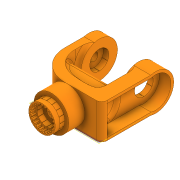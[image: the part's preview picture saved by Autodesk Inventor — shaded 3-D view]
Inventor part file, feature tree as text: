
AUTODESK INVENTOR PART (.ipt)
format: ipt  version: 2020 (Build 240168000, 168)  size: 1,737,216 bytes
history: native  units: in
note: dims shown in document units (in); Inventor stores cm internally (conversion verified against a paired STEP export)
features: sketch x34, extrude x33, projected_geometry x27, chamfer x5, plane x5, fillet x5
ambient origin geometry x8: Origin, YZ Plane, XZ Plane, XY Plane, X Axis, Y Axis, Z Axis, Center Point
bodies: Solid1 (feature_tree)
feature tree (109):
  extrude  "Extrusion1"  Depth=2.0472in
  extrude  "Extrusion2"  Depth=1.1024in
  chamfer  "Chamfer2"  Distance=0.2756in
  extrude  "Extrusion4"  Depth=0.0157in
  extrude  "Extrusion7"  Depth=0.2756in TaperAngle=0.0deg
  chamfer  "Chamfer4"  Distance=0.0394in
  extrude  "Extrusion8"  Depth=0.315in
  sketch  "Sketch12"  dims[d39=1.4567in d57=0.0394in d58=0.0in]
  plane  "Work Plane1"
  sketch  "Sketch13"  dims[d59=0.315in d60=0.125in d61=0.0137in d67=0.0157in]
  extrude  "Extrusion10"  Depth=0.0394in TaperAngle=0.0deg
  extrude  "Extrusion11"  Depth=0.0866in
  chamfer  "Chamfer5"  Distance=9.4488in Angle=360.0deg
  extrude  "Extrusion12"  Depth=0.2756in TaperAngle=0.0deg
  plane  "Work Plane2"
  extrude  "Extrusion13"  Depth=0.2756in
  plane  "Work Plane3"
  extrude  "Extrusion14"  Depth=1.0236in
  extrude  "Extrusion15"  Depth=0.8858in
  extrude  "Extrusion16"  Depth=0.3937in
  extrude  "Extrusion17"  Depth=1.378in
  sketch  "Sketch21"  dims[d107=0.2756in d108=0.0in d109=0.2756in d110=0.125in d111=0.0137in]
  extrude  "Extrusion19"  Depth=0.5906in
  sketch  "Sketch23"  dims[d112=1.0in d113=0.0in d114=1.0236in]
  extrude  "Extrusion20"  Depth=0.1575in TaperAngle=0.0deg
  extrude  "Extrusion21"  Depth=0.1575in TaperAngle=0.0deg
  extrude  "Extrusion22"  Depth=4.2323in
  extrude  "Extrusion23"  Depth=0.1575in
  extrude  "Extrusion24"  Depth=1.1024in
  extrude  "Extrusion25"  Depth=0.4921in
  extrude  "Extrusion26"  Depth=0.75in
  extrude  "Extrusion27"  Depth=0.1575in TaperAngle=0.0deg
  extrude  "Extrusion28"  Depth=0.1575in
  extrude  "Extrusion29"  Depth=0.1575in
  plane  "Work Plane4"
  extrude  "Extrusion30"  Depth=0.315in TaperAngle=0.0deg
  fillet  "Fillet1"  Radius=0.3937in
  fillet  "Fillet2"  Radius=0.315in
  extrude  "Extrusion31"  Depth=0.315in TaperAngle=0.0deg
  extrude  "Extrusion32"  Depth=0.315in TaperAngle=0.0deg
  extrude  "Extrusion33"  Depth=0.3937in TaperAngle=0.0deg
  fillet  "Fillet3"  Radius=0.2165in
  extrude  "Extrusion34"  [1 undecoded]
  chamfer  "Chamfer6"  Distance=0.4724in
  chamfer  "Chamfer7"  Distance=0.2756in
  extrude  "Extrusion35"  Depth=0.315in
  extrude  "Extrusion36"  Depth=0.315in
  plane  "Work Plane5"
  fillet  "Fillet5"  Radius=0.0394in
  extrude  "Extrusion38"  Depth=0.315in TaperAngle=0.0deg
  extrude  "Extrusion39"  Depth=0.315in
  fillet  "Fillet6"  Radius=0.001in
  sketch  "Sketch1"  dims[d0=0.6299in d1=2.0472in]
  sketch  "Sketch2"  dims[d2=0.9449in d3=0.0in d4=1.1024in]
  sketch  "Sketch4"  dims[d5=1.5748in d6=0.2756in d7=0.0in]
  sketch  "Sketch8"  dims[d11=0.2756in d12=0.125in d13=0.0137in d25=0.0157in]
  projected_geometry  "Projected Loop2"
  sketch  "Sketch10"  dims[d26=6.2992in d28=360.0deg d30=0.2756in d31=0.0in]
  sketch  "Sketch14"  dims[d68=4.7244in d70=360.0deg d72=0.0394in d73=0.0in]
  sketch  "Sketch15"  dims[d83=0.0591in d84=0.0866in]
  projected_geometry  "Projected Loop4"
  sketch  "Sketch16"  dims[d85=0.0827in]
  sketch  "Sketch17"  dims[d86=0.0827in]
  projected_geometry  "Projected Loop5"
  sketch  "Sketch18"  dims[d87=0.0827in d88=9.4488in d90=360.0deg]
  projected_geometry  "Projected Loop6"
  projected_geometry  "Projected Loop7"
  sketch  "Sketch19"  dims[d92=0.2756in]
  projected_geometry  "Projected Loop8"
  projected_geometry  "Projected Loop9"
  sketch  "Sketch20"  dims[d94=9.4488in d95=0.0827in d96=0.0827in d97=0.0827in d98=360.0deg d105=0.2756in d106=0.0in]
  projected_geometry  "Projected Loop10"
  projected_geometry  "Projected Loop11"
  projected_geometry  "Projected Loop12"
  projected_geometry  "Projected Loop13"
  sketch  "Sketch25"  dims[d115=0.7874in d117=0.8858in]
  sketch  "Sketch26"  dims[d118=2.7559in d119=0.3937in]
  projected_geometry  "Projected Loop16"
  projected_geometry  "Projected Loop17"
  sketch  "Sketch27"  dims[d120=0.5906in d121=1.378in]
  projected_geometry  "Projected Loop18"
  projected_geometry  "Projected Loop19"
  sketch  "Sketch28"  dims[d123=3.4941in d124=0.5906in]
  projected_geometry  "Projected Loop20"
  projected_geometry  "Projected Loop21"
  sketch  "Sketch29"  dims[d126=1.9685in d129=0.1575in d130=0.0in]
  projected_geometry  "Projected Loop22"
  projected_geometry  "Projected Loop23"
  sketch  "Sketch30"  dims[d131=-2.0472in d132=0.1575in d133=0.0in]
  projected_geometry  "Projected Loop24"
  sketch  "Sketch31"  dims[d134=2.126in d136=4.2323in]
  sketch  "Sketch32"  dims[d137=0.1575in d138=0.1575in]
  sketch  "Sketch34"  dims[d139=0.4921in d140=0.0in d141=1.1024in]
  projected_geometry  "Projected Loop25"
  sketch  "Sketch35"  dims[d142=1.1614in d143=0.4921in]
  sketch  "Sketch36"  dims[d144=0.3445in d145=0.75in]
  projected_geometry  "Projected Loop26"
  sketch  "Sketch37"  dims[d146=0.1575in d147=0.0in d148=0.2165in d149=0.0in]
  projected_geometry  "Projected Loop27"
  sketch  "Sketch38"  dims[d152=1.0039in d153=0.0in d154=0.1575in]
  projected_geometry  "Projected Loop28"
  sketch  "Sketch39"  dims[d155=0.1575in d160=1.1811in]
  projected_geometry  "Projected Loop29"
  sketch  "Sketch40"  dims[d161=0.1969in d162=0.0in d163=0.315in d164=0.0in d165=0.3937in d166=0.0in d167=0.315in d168=0.0in]
  sketch  "Sketch41"  dims[d169=0.315in d170=0.0in d171=0.315in d172=0.0in]
  projected_geometry  "Projected Loop30"
  sketch  "Sketch43"  dims[d173=0.315in d174=0.0in d175=0.315in d176=0.0in]
  projected_geometry  "Projected Loop31"
  sketch  "Sketch44"  dims[d177=1.1024in d178=0.3937in d179=0.0in d180=0.2165in d181=0.0in d183=-0.0197in d184=0.4724in d185=0.2756in d186=0.0in d187=0.5512in d188=0.2165in d189=0.0394in d190=0.0in d191=0.0394in d192=0.0in d193=0.001in d194=0.001in d195=1.0in d196=0.0in d197=0.1575in d198=1.0in d199=0.0in d200=0.315in d201=0.125in d202=0.0137in d203=0.315in d204=0.125in d205=0.0137in d206=0.0157in d207=2.3622in d209=360.0deg d211=1.0in d212=0.0in d213=1.0in d214=0.0in d215=-0.0787in d221=0.1969in d222=0.1969in d223=0.0in d224=0.1575in d225=0.1575in d226=0.1969in d227=0.0in d228=0.315in]
note: 1 required parameter value undecoded (feature->parameter linkage not recoverable at this tier; creation-order binding heuristic only, values carry confidence <= 0.55)
